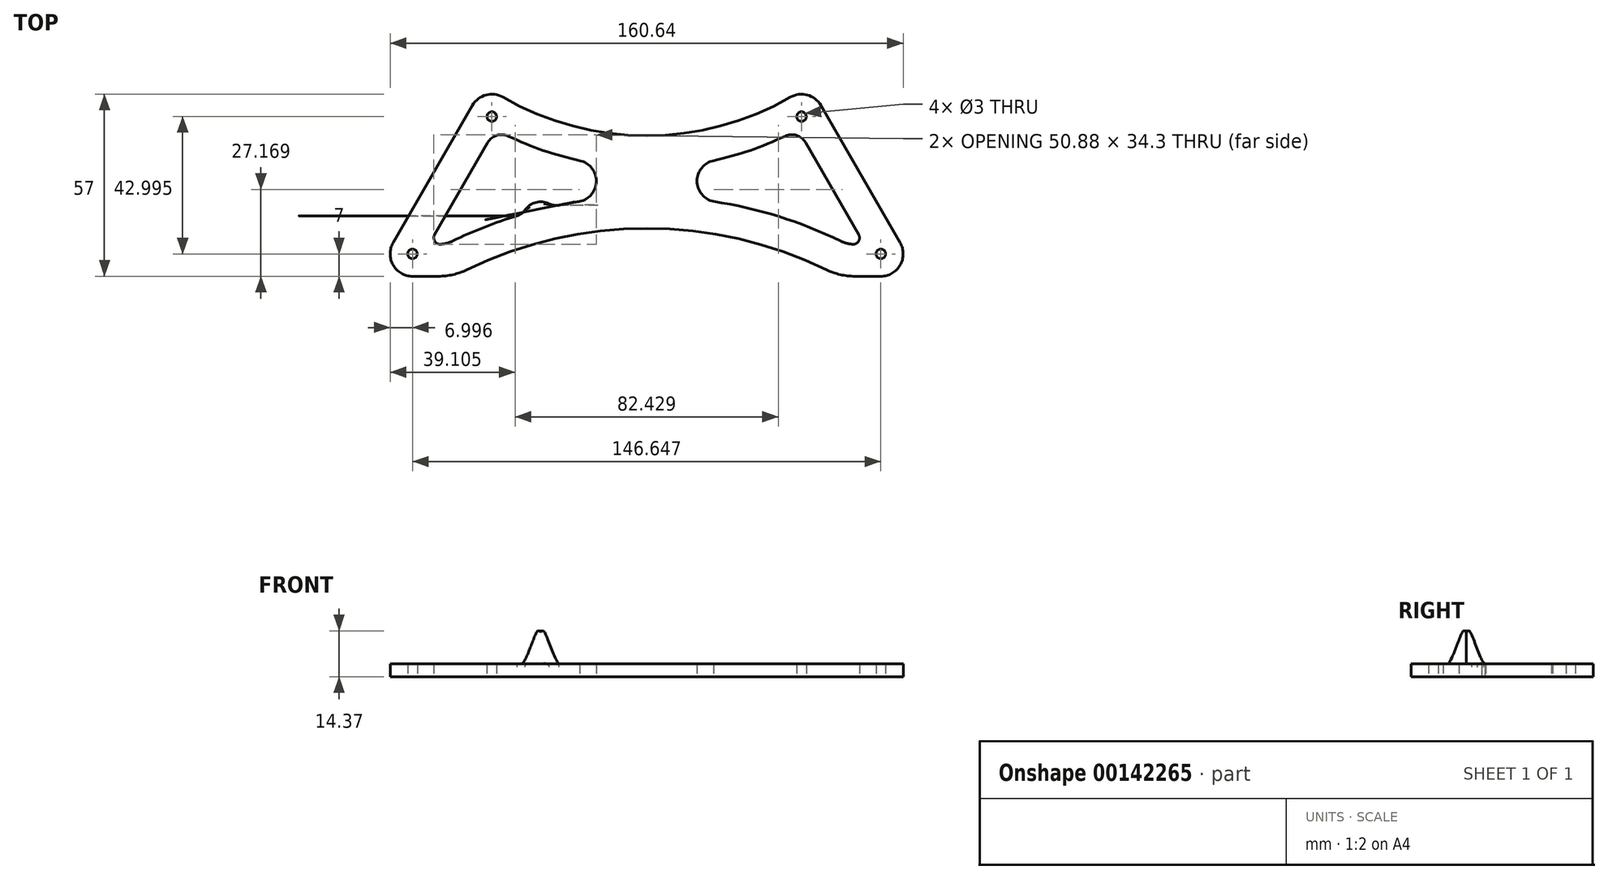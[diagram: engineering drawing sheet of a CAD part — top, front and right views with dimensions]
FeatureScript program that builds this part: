
annotation { "Feature Type Name" : "Feature", "Feature Type Description" : "" }
export const myFeature = defineFeature(function(context is Context, id is Id, definition is map)
    precondition{}
    {
        {
            var Q0;
            Q0=qCreatedBy(makeId("Top.planeOp"),FACE);
            var sketch = newSketch(context, id + "F0", { "sketchPlane" : qUnion([Q0])});
            skLineSegment(sketch, "E0", {"start": v(-143.18, 0) * mm, "end": v(0, 248) * mm});
            skLineSegment(sketch, "E1", {"start": v(0, 248) * mm, "end": v(143.18, 0) * mm});
            skLineSegment(sketch, "E2", {"start": v(143.18, 0) * mm, "end": v(-143.18, 0) * mm});
            skLineSegment(sketch, "E3", {"start": v(0, 248) * mm, "end": v(0, 0) * mm});
            skCircle(sketch, "E4", {"center": v(0, 0) * mm, "radius": 124 * mm});
            skLineSegment(sketch, "E5", {"start": v(-71.6, 124) * mm, "end": v(71.6, 124) * mm});
            skLineSegment(sketch, "E6.0", {"start": v(-73.32, 114) * mm, "end": v(-65.15, 114) * mm});
            skArc(sketch, "E7.0", {"start": v(-89.6, 92.8) * mm, "mid": v(0, -129) * mm, "end": v(89.6, 92.8) * mm});
            skLineSegment(sketch, "E8.0", {"start": v(-68.13, 139) * mm, "end": v(68.13, 139) * mm});
            skLineSegment(sketch, "E9.0", {"start": v(-79.39, 124.5) * mm, "end": v(-54.56, 167.5) * mm});
            skLineSegment(sketch, "E10.0", {"start": v(54.56, 167.5) * mm, "end": v(79.39, 124.5) * mm});
            skArc(sketch, "E11.filletArc", {"start": v(-68.13, 139) * mm, "mid": v(-70.63, 138.33) * mm, "end": v(-72.46, 136.5) * mm});
            skArc(sketch, "E12.filletArc", {"start": v(-79.39, 124.5) * mm, "mid": v(-79.39, 117.5) * mm, "end": v(-73.32, 114) * mm});
            skArc(sketch, "E13.filletArc", {"start": v(73.32, 114) * mm, "mid": v(79.39, 117.5) * mm, "end": v(79.39, 124.5) * mm});
            skArc(sketch, "E14.filletArc", {"start": v(72.46, 136.5) * mm, "mid": v(70.63, 138.33) * mm, "end": v(68.13, 139) * mm});
            skLineSegment(sketch, "E15.trimOffspring", {"start": v(65.15, 114) * mm, "end": v(73.32, 114) * mm});
            skArc(sketch, "E16.trimOffspring", {"start": v(56.4, 116.01) * mm, "mid": v(0, 129) * mm, "end": v(-56.4, 116.01) * mm});
            skPoint(sketch, "E17.visualSharp", {"position": v(-60.37, 114) * mm});
            skArc(sketch, "E17.filletArc", {"start": v(-65.15, 114) * mm, "mid": v(-60.67, 114.5) * mm, "end": v(-56.4, 116.01) * mm});
            skPoint(sketch, "E18.visualSharp", {"position": v(60.37, 114) * mm});
            skArc(sketch, "E18.filletArc", {"start": v(56.4, 116.01) * mm, "mid": v(60.67, 114.5) * mm, "end": v(65.15, 114) * mm});
            skArc(sketch, "E19", {"start": v(-45, 170.06) * mm, "mid": v(0, 158) * mm, "end": v(45, 170.06) * mm});
            skPoint(sketch, "E20.orphan", {"position": v(-45, 170.06) * mm});
            skPoint(sketch, "E21.orphan", {"position": v(45, 170.06) * mm});
            skPoint(sketch, "E22.visualSharp", {"position": v(-50.93, 173.8) * mm});
            skArc(sketch, "E22.filletArc", {"start": v(-45, 170.06) * mm, "mid": v(-50.31, 170.76) * mm, "end": v(-54.56, 167.5) * mm});
            skPoint(sketch, "E23.visualSharp", {"position": v(50.93, 173.8) * mm});
            skArc(sketch, "E23.filletArc", {"start": v(54.56, 167.5) * mm, "mid": v(50.31, 170.76) * mm, "end": v(45, 170.06) * mm});
            skArc(sketch, "E24.0", {"start": v(60.78, 125) * mm, "mid": v(0, 139) * mm, "end": v(-60.78, 125) * mm});
            skArc(sketch, "E24.1", {"start": v(60.78, 125) * mm, "mid": v(64.29, 124.04) * mm, "end": v(67.9, 124.39) * mm});
            skLineSegment(sketch, "E24.2", {"start": v(49.75, 155.83) * mm, "end": v(67.9, 124.39) * mm});
            skArc(sketch, "E24.3", {"start": v(-43.26, 157.84) * mm, "mid": v(0, 148) * mm, "end": v(43.26, 157.84) * mm});
            skArc(sketch, "E25", {"start": v(-20.95, 137.41) * mm, "mid": v(-15.78, 143.82) * mm, "end": v(-20.95, 150.22) * mm});
            skArc(sketch, "E26", {"start": v(20.95, 150.22) * mm, "mid": v(15.78, 143.82) * mm, "end": v(20.95, 137.41) * mm});
            skCircle(sketch, "E27", {"center": v(-48.5, 164) * mm, "radius": 1.5 * mm});
            skCircle(sketch, "E28", {"center": v(48.5, 164) * mm, "radius": 1.5 * mm});
            skCircle(sketch, "E29", {"center": v(-73.32, 121) * mm, "radius": 1.5 * mm});
            skCircle(sketch, "E30", {"center": v(73.32, 121) * mm, "radius": 1.5 * mm});
            skArc(sketch, "E31.0", {"start": v(-65.15, 124) * mm, "mid": v(-62.91, 124.25) * mm, "end": v(-60.78, 125) * mm});
            skLineSegment(sketch, "E32.trimOffspring", {"start": v(-68.13, 124) * mm, "end": v(-49.75, 155.83) * mm});
            skPoint(sketch, "E33.visualSharp", {"position": v(-47.38, 159.94) * mm});
            skArc(sketch, "E33.filletArc", {"start": v(-43.26, 157.84) * mm, "mid": v(-46.9, 158.1) * mm, "end": v(-49.75, 155.83) * mm});
            skPoint(sketch, "E34.visualSharp", {"position": v(47.38, 159.94) * mm});
            skArc(sketch, "E34.filletArc", {"start": v(49.75, 155.83) * mm, "mid": v(46.9, 158.1) * mm, "end": v(43.26, 157.84) * mm});
            skSolve(sketch);
        }
        {
            var Q0;
            {var subQ0=sQuery(id+"F0.wireOp",EDGE,"E5");var subQ1=sQuery(id+"F0.wireOp",EDGE,"E0");var subQ2=makeQuery(id+"F0.imprint","INTERSECT",VERTEX,{"derivedFrom":[subQ1,subQ0]});Q0=makeQuery(id+"F0.imprint","IMPRINT",FACE,{"disambiguationData":[TD([[makeQuery(id+"F0.imprint","IMPRINT",EDGE,{"disambiguationData":[TD([[subQ2,-1.0]])],"derivedFrom":subQ1}),-1.0]])]});}
            var Q1;
            {var subQ10=sQuery(id+"F0.wireOp",EDGE,"E6.0");Q1=makeQuery(id+"F0.imprint","IMPRINT",FACE,{"disambiguationData":[TD([[makeQuery(id+"F0.imprint","IMPRINT",EDGE,{"derivedFrom":subQ10}),1.0]])]});}
            var Q2;
            {var subQ2=sQuery(id+"F0.wireOp",EDGE,"E11.filletArc");Q2=makeQuery(id+"F0.imprint","IMPRINT",FACE,{"disambiguationData":[TD([[makeQuery(id+"F0.imprint","IMPRINT",EDGE,{"derivedFrom":subQ2}),-1.0]])]});}
            var Q3;
            {var subQ3=sQuery(id+"F0.wireOp",EDGE,"E5");var subQ6=sQuery(id+"F0.wireOp",EDGE,"E1");var subQ9=makeQuery(id+"F0.imprint","INTERSECT",VERTEX,{"derivedFrom":[subQ6,subQ3]});Q3=makeQuery(id+"F0.imprint","IMPRINT",FACE,{"disambiguationData":[TD([[makeQuery(id+"F0.imprint","IMPRINT",EDGE,{"disambiguationData":[TD([[subQ9,1.0]])],"derivedFrom":subQ6}),-1.0]])]});}
            var Q4;
            {var subQ12=sQuery(id+"F0.wireOp",EDGE,"E15.trimOffspring");Q4=makeQuery(id+"F0.imprint","IMPRINT",FACE,{"disambiguationData":[TD([[makeQuery(id+"F0.imprint","IMPRINT",EDGE,{"derivedFrom":subQ12}),1.0]])]});}
            var Q5;
            {var subQ2=sQuery(id+"F0.wireOp",EDGE,"E14.filletArc");Q5=makeQuery(id+"F0.imprint","IMPRINT",FACE,{"disambiguationData":[TD([[makeQuery(id+"F0.imprint","IMPRINT",EDGE,{"derivedFrom":subQ2}),-1.0]])]});}
            var Q6;
            {var subQ0=sQuery(id+"F0.wireOp",EDGE,"E11.filletArc");Q6=makeQuery(id+"F0.imprint","IMPRINT",FACE,{"disambiguationData":[TD([[makeQuery(id+"F0.imprint","IMPRINT",EDGE,{"derivedFrom":subQ0}),1.0]])]});}
            var Q7;
            {var subQ0=sQuery(id+"F0.wireOp",EDGE,"E14.filletArc");Q7=makeQuery(id+"F0.imprint","IMPRINT",FACE,{"disambiguationData":[TD([[makeQuery(id+"F0.imprint","IMPRINT",EDGE,{"derivedFrom":subQ0}),1.0]])]});}
            var Q8;
            {var subQ15=sQuery(id+"F0.wireOp",EDGE,"E34.filletArc");Q8=makeQuery(id+"F0.imprint","IMPRINT",FACE,{"disambiguationData":[TD([[makeQuery(id+"F0.imprint","IMPRINT",EDGE,{"derivedFrom":subQ15}),-1.0]])]});}
            var Q9;
            {var subQ0=sQuery(id+"F0.wireOp",EDGE,"E26");var subQ3=sQuery(id+"F0.wireOp",EDGE,"E24.0");var subQ5=makeQuery(id+"F0.imprint","INTERSECT",VERTEX,{"derivedFrom":[subQ3,subQ0]});Q9=makeQuery(id+"F0.imprint","IMPRINT",FACE,{"disambiguationData":[TD([[makeQuery(id+"F0.imprint","IMPRINT",EDGE,{"disambiguationData":[TD([[subQ5,1.0]])],"derivedFrom":subQ0}),-1.0]])]});}
            var Q10;
            {var subQ0=sQuery(id+"F0.wireOp",EDGE,"E25");var subQ3=sQuery(id+"F0.wireOp",EDGE,"E24.0");var subQ5=makeQuery(id+"F0.imprint","INTERSECT",VERTEX,{"derivedFrom":[subQ3,subQ0]});Q10=makeQuery(id+"F0.imprint","IMPRINT",FACE,{"disambiguationData":[TD([[makeQuery(id+"F0.imprint","IMPRINT",EDGE,{"disambiguationData":[TD([[subQ5,-1.0]])],"derivedFrom":subQ0}),-1.0]])]});}
            var Q11;
            {var subQ5=sQuery(id+"F0.wireOp",EDGE,"E31.0");Q11=makeQuery(id+"F0.imprint","IMPRINT",FACE,{"disambiguationData":[TD([[makeQuery(id+"F0.imprint","IMPRINT",EDGE,{"derivedFrom":subQ5}),-1.0]])]});}
            var Q12;
            {var subQ0=sQuery(id+"F0.wireOp",EDGE,"E16.trimOffspring");var subQ3=sQuery(id+"F0.wireOp",EDGE,"E5");var subQ4=makeQuery(id+"F0.imprint","INTERSECT",VERTEX,{"disambiguationData":[OD(1.0)],"derivedFrom":[subQ3,subQ0]});Q12=makeQuery(id+"F0.imprint","IMPRINT",FACE,{"disambiguationData":[TD([[makeQuery(id+"F0.imprint","IMPRINT",EDGE,{"disambiguationData":[TD([[subQ4,-1.0]])],"derivedFrom":subQ3}),1.0]])]});}
            var Q13;
            {var subQ14=sQuery(id+"F0.wireOp",EDGE,"E33.filletArc");Q13=makeQuery(id+"F0.imprint","IMPRINT",FACE,{"disambiguationData":[TD([[makeQuery(id+"F0.imprint","IMPRINT",EDGE,{"derivedFrom":subQ14}),-1.0]])]});}
            var Q14;
            {var subQ0=sQuery(id+"F0.wireOp",EDGE,"E24.3");var subQ5=sQuery(id+"F0.wireOp",EDGE,"E25");var subQ7=makeQuery(id+"F0.imprint","INTERSECT",VERTEX,{"derivedFrom":[subQ0,subQ5]});Q14=makeQuery(id+"F0.imprint","IMPRINT",FACE,{"disambiguationData":[TD([[makeQuery(id+"F0.imprint","IMPRINT",EDGE,{"disambiguationData":[TD([[subQ7,-1.0]])],"derivedFrom":subQ0}),-1.0]])]});}
            var Q15;
            {var subQ0=sQuery(id+"F0.wireOp",EDGE,"E24.3");var subQ5=sQuery(id+"F0.wireOp",EDGE,"E26");var subQ7=makeQuery(id+"F0.imprint","INTERSECT",VERTEX,{"derivedFrom":[subQ0,subQ5]});Q15=makeQuery(id+"F0.imprint","IMPRINT",FACE,{"disambiguationData":[TD([[makeQuery(id+"F0.imprint","IMPRINT",EDGE,{"disambiguationData":[TD([[subQ7,1.0]])],"derivedFrom":subQ0}),-1.0]])]});}
            extrude(context, id + "F1", {"entities" : qUnion([Q0, Q1, Q2, Q3, Q4, Q5, Q6, Q7, Q8, Q9, Q10, Q11, Q12, Q13, Q14, Q15]), "depth" : 4 * mm});
        }
        {
            var Q0;
            Q0=makeQuery(id+"F1.opExtrude","CAP_FACE",FACE,{"disambiguationData":[OSD([sQuery(id+"F0.wireOp",EDGE,"E6.0"),sQuery(id+"F0.wireOp",EDGE,"E8.0"),sQuery(id+"F0.wireOp",EDGE,"E9.0"),sQuery(id+"F0.wireOp",EDGE,"E10.0"),sQuery(id+"F0.wireOp",EDGE,"2ZfsWljG-NP00-yzqO-WBOH-db8kQLTk2yTH"),sQuery(id+"F0.wireOp",EDGE,"zZSjXf2h-otWV-leoM-h0kO-TShHnwcGzjZo"),sQuery(id+"F0.wireOp",EDGE,"5KSrMAXx-vpK0-kglo-bSC1-R4JIMw2FEGv5"),sQuery(id+"F0.wireOp",EDGE,"jQOIPKL7-3Q37-fATC-nByG-EZj9iEGbSLed"),sQuery(id+"F0.wireOp",EDGE,"E11.filletArc"),sQuery(id+"F0.wireOp",EDGE,"E12.filletArc"),sQuery(id+"F0.wireOp",EDGE,"E13.filletArc"),sQuery(id+"F0.wireOp",EDGE,"E14.filletArc"),sQuery(id+"F0.wireOp",EDGE,"E15.trimOffspring"),sQuery(id+"F0.wireOp",EDGE,"E16.trimOffspring"),sQuery(id+"F0.wireOp",EDGE,"E17.filletArc"),sQuery(id+"F0.wireOp",EDGE,"E18.filletArc")])],"isStart":false});
            var sketch = newSketch(context, id + "F2", { "sketchPlane" : qUnion([Q0])});
            skLineSegment(sketch, "E35", {"start": v(-66.89, 132.15) * mm, "end": v(66.89, 132.15) * mm});
            skLineSegment(sketch, "E36", {"start": v(-73.89, 120.02) * mm, "end": v(73.89, 120.02) * mm});
            skLineSegment(sketch, "E37", {"start": v(-66.89, 139) * mm, "end": v(-66.89, 120.02) * mm});
            skLineSegment(sketch, "E38", {"start": v(66.89, 132.15) * mm, "end": v(66.89, 120.02) * mm});
            skLineSegment(sketch, "E39.1.0.0", {"start": v(-61.89, 139) * mm, "end": v(-61.89, 120.02) * mm});
            skLineSegment(sketch, "E39.2.0.0", {"start": v(-56.89, 139) * mm, "end": v(-56.89, 120.02) * mm});
            skLineSegment(sketch, "E39.3.0.0", {"start": v(-51.89, 139) * mm, "end": v(-51.89, 120.02) * mm});
            skLineSegment(sketch, "E39.4.0.0", {"start": v(-46.89, 139) * mm, "end": v(-46.89, 120.02) * mm});
            skLineSegment(sketch, "E39.5.0.0", {"start": v(-41.89, 139) * mm, "end": v(-41.89, 120.02) * mm});
            skLineSegment(sketch, "E39.6.0.0", {"start": v(-36.89, 139) * mm, "end": v(-36.89, 120.02) * mm});
            skLineSegment(sketch, "E39.7.0.0", {"start": v(-31.89, 139) * mm, "end": v(-31.89, 120.02) * mm});
            skLineSegment(sketch, "E39.8.0.0", {"start": v(-26.89, 139) * mm, "end": v(-26.89, 120.02) * mm});
            skLineSegment(sketch, "E39.9.0.0", {"start": v(-21.89, 139) * mm, "end": v(-21.89, 120.02) * mm});
            skLineSegment(sketch, "E39.direction1", {"start": v(-66.89, 120.02) * mm, "end": v(-61.89, 120.02) * mm, "construction": true});
            skLineSegment(sketch, "E40.0", {"start": v(-68.13, 139) * mm, "end": v(68.13, 139) * mm});
            skPoint(sketch, "E41.orphan", {"position": v(-61.89, 132.15) * mm});
            skPoint(sketch, "E42.orphan", {"position": v(-56.89, 132.15) * mm});
            skPoint(sketch, "E43.orphan", {"position": v(-51.89, 132.15) * mm});
            skPoint(sketch, "E44.orphan", {"position": v(-46.89, 132.15) * mm});
            skPoint(sketch, "E45.orphan", {"position": v(-41.89, 132.15) * mm});
            skPoint(sketch, "E46.orphan", {"position": v(-36.89, 132.15) * mm});
            skPoint(sketch, "E47.orphan", {"position": v(-31.89, 132.15) * mm});
            skPoint(sketch, "E48.orphan", {"position": v(-26.89, 132.15) * mm});
            skPoint(sketch, "E49.orphan", {"position": v(-21.89, 132.15) * mm});
            skLineSegment(sketch, "E50.1.0.0", {"start": v(-16.89, 139) * mm, "end": v(-16.89, 120.02) * mm});
            skLineSegment(sketch, "E50.2.0.0", {"start": v(-11.89, 139) * mm, "end": v(-11.89, 120.02) * mm});
            skLineSegment(sketch, "E50.3.0.0", {"start": v(-6.89, 139) * mm, "end": v(-6.89, 120.02) * mm});
            skLineSegment(sketch, "E50.4.0.0", {"start": v(-1.89, 139) * mm, "end": v(-1.89, 120.02) * mm});
            skLineSegment(sketch, "E50.5.0.0", {"start": v(3.11, 139) * mm, "end": v(3.11, 120.02) * mm});
            skLineSegment(sketch, "E50.6.0.0", {"start": v(8.11, 139) * mm, "end": v(8.11, 120.02) * mm});
            skLineSegment(sketch, "E50.7.0.0", {"start": v(13.11, 139) * mm, "end": v(13.11, 120.02) * mm});
            skLineSegment(sketch, "E50.8.0.0", {"start": v(18.11, 139) * mm, "end": v(18.11, 120.02) * mm});
            skLineSegment(sketch, "E50.9.0.0", {"start": v(23.11, 139) * mm, "end": v(23.11, 120.02) * mm});
            skLineSegment(sketch, "E50.direction1", {"start": v(-21.89, 120.02) * mm, "end": v(-16.89, 120.02) * mm, "construction": true});
            skLineSegment(sketch, "E51.direction2", {"start": v(-66.89, 132.15) * mm, "end": v(-61.89, 132.17) * mm, "construction": true});
            skLineSegment(sketch, "E52", {"start": v(-66.89, 134.15) * mm, "end": v(23.11, 134.15) * mm});
            skLineSegment(sketch, "E53.1.0.0", {"start": v(-66.89, 130.15) * mm, "end": v(66.89, 130.15) * mm});
            skLineSegment(sketch, "E53.2.0.0", {"start": v(-66.89, 128.15) * mm, "end": v(66.89, 128.15) * mm});
            skLineSegment(sketch, "E53.3.0.0", {"start": v(-66.89, 126.15) * mm, "end": v(66.89, 126.15) * mm});
            skLineSegment(sketch, "E53.4.0.0", {"start": v(-66.89, 124.14) * mm, "end": v(66.89, 124.14) * mm});
            skLineSegment(sketch, "E53.direction1", {"start": v(-66.89, 132.15) * mm, "end": v(-66.89, 130.15) * mm, "construction": true});
            skLineSegment(sketch, "E54", {"start": v(-64.39, 139) * mm, "end": v(-64.39, 120.02) * mm});
            skLineSegment(sketch, "E55.1.0.0", {"start": v(-59.39, 139) * mm, "end": v(-59.39, 120.02) * mm});
            skLineSegment(sketch, "E55.2.0.0", {"start": v(-54.39, 139) * mm, "end": v(-54.39, 120.02) * mm});
            skLineSegment(sketch, "E55.3.0.0", {"start": v(-49.39, 139) * mm, "end": v(-49.39, 120.02) * mm});
            skLineSegment(sketch, "E55.4.0.0", {"start": v(-44.39, 139) * mm, "end": v(-44.39, 120.02) * mm});
            skLineSegment(sketch, "E55.5.0.0", {"start": v(-39.39, 139) * mm, "end": v(-39.39, 120.02) * mm});
            skLineSegment(sketch, "E55.6.0.0", {"start": v(-34.39, 139) * mm, "end": v(-34.39, 120.02) * mm});
            skLineSegment(sketch, "E55.7.0.0", {"start": v(-29.39, 139) * mm, "end": v(-29.39, 120.02) * mm});
            skLineSegment(sketch, "E55.8.0.0", {"start": v(-24.39, 139) * mm, "end": v(-24.39, 120.02) * mm});
            skLineSegment(sketch, "E55.9.0.0", {"start": v(-19.39, 139) * mm, "end": v(-19.39, 120.02) * mm});
            skLineSegment(sketch, "E55.direction1", {"start": v(-64.39, 120.02) * mm, "end": v(-59.39, 120.02) * mm, "construction": true});
            skLineSegment(sketch, "E56.1.0.0", {"start": v(-14.39, 139) * mm, "end": v(-14.39, 120.02) * mm});
            skLineSegment(sketch, "E56.2.0.0", {"start": v(-9.39, 139) * mm, "end": v(-9.39, 120.02) * mm});
            skLineSegment(sketch, "E56.3.0.0", {"start": v(-4.39, 139) * mm, "end": v(-4.39, 120.02) * mm});
            skLineSegment(sketch, "E56.4.0.0", {"start": v(0.61, 139) * mm, "end": v(0.61, 120.02) * mm});
            skLineSegment(sketch, "E56.5.0.0", {"start": v(5.61, 139) * mm, "end": v(5.61, 120.02) * mm});
            skLineSegment(sketch, "E56.6.0.0", {"start": v(10.61, 139) * mm, "end": v(10.61, 120.02) * mm});
            skLineSegment(sketch, "E56.7.0.0", {"start": v(15.61, 139) * mm, "end": v(15.61, 120.02) * mm});
            skLineSegment(sketch, "E56.8.0.0", {"start": v(20.61, 139) * mm, "end": v(20.61, 120.02) * mm});
            skLineSegment(sketch, "E56.9.0.0", {"start": v(25.61, 139) * mm, "end": v(25.61, 120.02) * mm});
            skLineSegment(sketch, "E56.direction1", {"start": v(-19.39, 120.02) * mm, "end": v(-14.39, 120.02) * mm, "construction": true});
            skLineSegment(sketch, "E57", {"start": v(-66.89, 136.15) * mm, "end": v(23.11, 136.15) * mm});
            skSolve(sketch);
        }
        {
            var Q0;
            Q0=makeQuery(id+"FXNAXLt5MWnWNz7_1.opExtrude","CAP_FACE",FACE,{"disambiguationData":[OSD([sQuery(id+"F2.wireOp",EDGE,"E35"),sQuery(id+"F2.wireOp",EDGE,"E39.7.0.0"),sQuery(id+"F2.wireOp",EDGE,"E53.1.0.0"),sQuery(id+"F2.wireOp",EDGE,"E55.6.0.0")])],"isStart":false});
            var sketch = newSketch(context, id + "F3", { "sketchPlane" : qUnion([Q0])});
            skSolve(sketch);
        }
        {
            var Q0;
            Q0=makeQuery(id+"F1.opExtrude","CAP_FACE",FACE,{"disambiguationData":[OSD([sQuery(id+"F0.wireOp",EDGE,"E6.0"),sQuery(id+"F0.wireOp",EDGE,"E8.0"),sQuery(id+"F0.wireOp",EDGE,"E9.0"),sQuery(id+"F0.wireOp",EDGE,"E10.0"),sQuery(id+"F0.wireOp",EDGE,"2ZfsWljG-NP00-yzqO-WBOH-db8kQLTk2yTH"),sQuery(id+"F0.wireOp",EDGE,"zZSjXf2h-otWV-leoM-h0kO-TShHnwcGzjZo"),sQuery(id+"F0.wireOp",EDGE,"5KSrMAXx-vpK0-kglo-bSC1-R4JIMw2FEGv5"),sQuery(id+"F0.wireOp",EDGE,"jQOIPKL7-3Q37-fATC-nByG-EZj9iEGbSLed"),sQuery(id+"F0.wireOp",EDGE,"E11.filletArc"),sQuery(id+"F0.wireOp",EDGE,"E12.filletArc"),sQuery(id+"F0.wireOp",EDGE,"E13.filletArc"),sQuery(id+"F0.wireOp",EDGE,"E14.filletArc"),sQuery(id+"F0.wireOp",EDGE,"E15.trimOffspring"),sQuery(id+"F0.wireOp",EDGE,"E16.trimOffspring"),sQuery(id+"F0.wireOp",EDGE,"E17.filletArc"),sQuery(id+"F0.wireOp",EDGE,"E18.filletArc")])],"isStart":false});
            var sketch = newSketch(context, id + "F4", { "sketchPlane" : qUnion([Q0])});
            skLineSegment(sketch, "E58", {"start": v(-66.21, 132.56) * mm, "end": v(-33.21, 132.56) * mm});
            skLineSegment(sketch, "E59", {"start": v(-33.21, 131.3) * mm, "end": v(-33.21, 132.56) * mm});
            skCircle(sketch, "E60", {"center": v(-33.21, 131.3) * mm, "radius": 1 * mm});
            skCircle(sketch, "E61", {"center": v(-33.21, 131.3) * mm, "radius": 6 * mm});
            skSolve(sketch);
        }
        {
            var Q0;
            Q0 = qSketchRegion(id + "F4", true);
            var Q1;
            Q1=makeQuery(id+"F1.opExtrude","CAP_FACE",FACE,{"disambiguationData":[OSD([sQuery(id+"F0.wireOp",EDGE,"E5"),sQuery(id+"F0.wireOp",EDGE,"E6.0"),sQuery(id+"F0.wireOp",EDGE,"E9.0"),sQuery(id+"F0.wireOp",EDGE,"E10.0"),sQuery(id+"F0.wireOp",EDGE,"E12.filletArc"),sQuery(id+"F0.wireOp",EDGE,"E13.filletArc"),sQuery(id+"F0.wireOp",EDGE,"E15.trimOffspring"),sQuery(id+"F0.wireOp",EDGE,"E16.trimOffspring"),sQuery(id+"F0.wireOp",EDGE,"E17.filletArc"),sQuery(id+"F0.wireOp",EDGE,"E18.filletArc"),sQuery(id+"F0.wireOp",EDGE,"E19"),sQuery(id+"F0.wireOp",EDGE,"E22.filletArc"),sQuery(id+"F0.wireOp",EDGE,"E23.filletArc"),sQuery(id+"F0.wireOp",EDGE,"E24.0"),sQuery(id+"F0.wireOp",EDGE,"E24.1"),sQuery(id+"F0.wireOp",EDGE,"E24.2"),sQuery(id+"F0.wireOp",EDGE,"E24.3"),sQuery(id+"F0.wireOp",EDGE,"E25"),sQuery(id+"F0.wireOp",EDGE,"E26"),sQuery(id+"F0.wireOp",EDGE,"E27"),sQuery(id+"F0.wireOp",EDGE,"E28"),sQuery(id+"F0.wireOp",EDGE,"E29"),sQuery(id+"F0.wireOp",EDGE,"E30"),sQuery(id+"F0.wireOp",EDGE,"E31.0"),sQuery(id+"F0.wireOp",EDGE,"E32.trimOffspring"),sQuery(id+"F0.wireOp",EDGE,"E33.filletArc"),sQuery(id+"F0.wireOp",EDGE,"E34.filletArc")])],"isStart":true});
            extrude(context, id + "F5", {"entities" : qUnion([Q0]), "operationType" : NewBodyOperationType.ADD, "endBound" : BoundingType.UP_TO_SURFACE, "oppositeDirection" : true, "endBoundEntityFace" : qUnion([Q1]), "depth" : 25 * mm});
        }
        {
            var Q0;
            Q0=sQuery(id+"F4.wireOp",VERTEX,"E61.center");
            var Q1;
            Q1=qCreatedBy(makeId("Front.planeOp"),FACE);
            cPlane(context, id + "F6", {"entities" : qUnion([Q0, Q1]), "cplaneType" : CPlaneType.PLANE_POINT, "offset" : 25 * mm, "width" : 150 * mm, "height" : 150 * mm});
        }
        {
            var Q0;
            Q0=qCreatedBy(id+"F6.planeOp",FACE);
            var sketch = newSketch(context, id + "F7", { "sketchPlane" : qUnion([Q0])});
            skLineSegment(sketch, "E62", {"start": v(-33.21, 14) * mm, "end": v(-33.21, 4) * mm});
            skLineSegment(sketch, "E63", {"start": v(-32.21, 4) * mm, "end": v(-32.21, 14.3) * mm});
            skLineSegment(sketch, "E64.0", {"start": v(-34.21, 4) * mm, "end": v(-32.21, 4) * mm});
            skFitSpline(sketch, "E65", {"points": [v(-33.21, 14) * mm, v(-32.21, 14.3) * mm, v(-27.21, 4) * mm], "startDerivative": vector(7.65, 0.34) * mm, "endDerivative": vector(5.26, 0) * mm});
            skLineSegment(sketch, "E66.0", {"start": v(-39.21, 4) * mm, "end": v(-27.21, 4) * mm});
            skLineSegment(sketch, "E67", {"start": v(-32.21, 4) * mm, "end": v(-32.21, 1) * mm});
            skLineSegment(sketch, "E68", {"start": v(-32.21, 1) * mm, "end": v(-33.21, 1) * mm});
            skLineSegment(sketch, "E69", {"start": v(-33.21, 1) * mm, "end": v(-33.21, 4) * mm});
            skSolve(sketch);
        }
        {
            var Q0;
            {var subQ0=sQuery(id+"F7.wireOp",EDGE,"E63");Q0=makeQuery(id+"F7.imprint","IMPRINT",FACE,{"disambiguationData":[TD([[makeQuery(id+"F7.imprint","IMPRINT",EDGE,{"derivedFrom":subQ0}),-1.0]])]});}
            var Q1;
            {var subQ0=sQuery(id+"F7.wireOp",EDGE,"E62");Q1=makeQuery(id+"F7.imprint","IMPRINT",FACE,{"disambiguationData":[TD([[makeQuery(id+"F7.imprint","IMPRINT",EDGE,{"derivedFrom":subQ0}),1.0]])]});}
            var Q2;
            Q2=sQuery(id+"F7.wireOp",EDGE,"E62");
            revolve(context, id + "F8", {"operationType" : NewBodyOperationType.ADD, "entities" : qUnion([Q0, Q1]), "axis" : qUnion([Q2]), "revolveType" : RevolveType.FULL});
        }
        {
            var Q0;
            Q0=makeQuery(id+"F8.boolean.opBoolean","MERGE",EDGE,{"derivedFrom":[makeQuery(id+"F5.opExtrude","CAP_EDGE",EDGE,{"disambiguationData":[OSD([sQuery(id+"F4.wireOp",EDGE,"E61")])],"isStart":true}),makeQuery(id+"F8.opRevolve","SWEPT_EDGE",EDGE,{"disambiguationData":[OSD([sQuery(id+"F7.wireOp",EDGE,"E65"),sQuery(id+"F7.wireOp",EDGE,"E66.0")])]})]});
            fillet(context, id + "F9", {"entities" : qUnion([Q0]), "radius" : 2 * mm, "tangentPropagation" : true, "allowEdgeOverflow" : false});
        }
        {
            var Q0;
            {var subQ0=sQuery(id+"F0.wireOp",EDGE,"E24.0");Q0=makeQuery(id+"F5.boolean.opBoolean","INTERSECT",EDGE,{"disambiguationData":[OD(0.0)],"derivedFrom":[makeQuery(id+"F1.opExtrude","SWEPT_FACE",FACE,{"disambiguationData":[OSD([subQ0]),TDD([makeQuery(id+"F0.imprint","IMPRINT",EDGE,{"disambiguationData":[TD([[makeQuery(id+"F0.imprint","INTERSECT",VERTEX,{"derivedFrom":[subQ0,sQuery(id+"F0.wireOp",EDGE,"E31.0")]}),1.0]])],"derivedFrom":subQ0})])]}),makeQuery(id+"F5.opExtrude","SWEPT_FACE",FACE,{"disambiguationData":[OSD([sQuery(id+"F4.wireOp",EDGE,"E61")])]})]});}
            var Q1;
            {var subQ0=sQuery(id+"F0.wireOp",EDGE,"E24.0");Q1=makeQuery(id+"F5.boolean.opBoolean","INTERSECT",EDGE,{"disambiguationData":[OD(1.0)],"derivedFrom":[makeQuery(id+"F1.opExtrude","SWEPT_FACE",FACE,{"disambiguationData":[OSD([subQ0]),TDD([makeQuery(id+"F0.imprint","IMPRINT",EDGE,{"disambiguationData":[TD([[makeQuery(id+"F0.imprint","INTERSECT",VERTEX,{"derivedFrom":[subQ0,sQuery(id+"F0.wireOp",EDGE,"E31.0")]}),1.0]])],"derivedFrom":subQ0})])]}),makeQuery(id+"F5.opExtrude","SWEPT_FACE",FACE,{"disambiguationData":[OSD([sQuery(id+"F4.wireOp",EDGE,"E61")])]})]});}
            fillet(context, id + "F10", {"entities" : qUnion([Q0, Q1]), "radius" : 5 * mm, "tangentPropagation" : true, "allowEdgeOverflow" : false});
        }
        {
            var Q0;
            Q0=makeQuery(id+"F1.opExtrude","SWEPT_EDGE",EDGE,{"disambiguationData":[OSD([sQuery(id+"F0.wireOp",EDGE,"E5"),sQuery(id+"F0.wireOp",EDGE,"E32.trimOffspring")])]});
            var Q1;
            Q1=makeQuery(id+"F1.opExtrude","SWEPT_EDGE",EDGE,{"disambiguationData":[OSD([sQuery(id+"F0.wireOp",EDGE,"E24.1"),sQuery(id+"F0.wireOp",EDGE,"E24.2")])]});
            fillet(context, id + "F11", {"entities" : qUnion([Q0, Q1]), "radius" : 2 * mm, "tangentPropagation" : true, "allowEdgeOverflow" : false});
        }
    });
